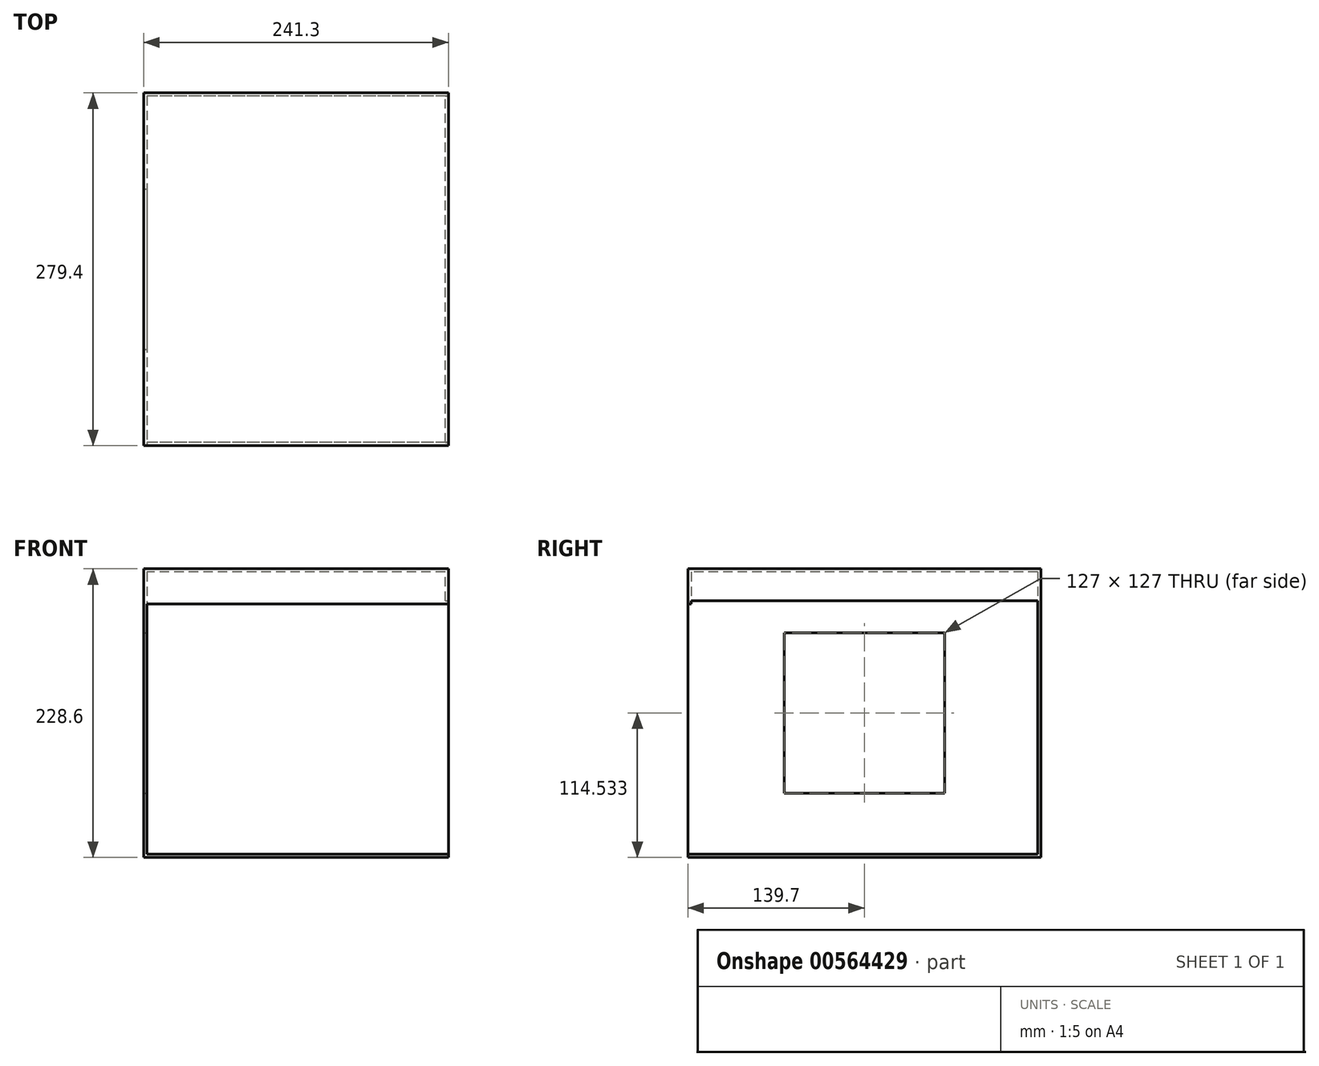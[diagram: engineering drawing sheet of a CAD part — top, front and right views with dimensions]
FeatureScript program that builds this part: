
annotation { "Feature Type Name" : "Feature", "Feature Type Description" : "" }
export const myFeature = defineFeature(function(context is Context, id is Id, definition is map)
    precondition{}
    {
        {
            var Q0;
            Q0=qCreatedBy(makeId("Top.planeOp"),FACE);
            var sketch = newSketch(context, id + "F0", { "sketchPlane" : qUnion([Q0])});
            skLineSegment(sketch, "E0.bottom", {"start": v(120.65, 139.7) * mm, "end": v(-120.65, 139.7) * mm});
            skLineSegment(sketch, "E0.top", {"start": v(120.65, -139.7) * mm, "end": v(-120.65, -139.7) * mm});
            skLineSegment(sketch, "E0.left", {"start": v(120.65, 139.7) * mm, "end": v(120.65, -139.7) * mm});
            skLineSegment(sketch, "E0.right", {"start": v(-120.65, 139.7) * mm, "end": v(-120.65, -139.7) * mm});
            skPoint(sketch, "E0.middle", {"position": v(0, 0) * mm});
            skSolve(sketch);
        }
        {
            var Q0;
            Q0 = qSketchRegion(id + "F0", true);
            extrude(context, id + "F1", {"entities" : qUnion([Q0]), "depth" : 228.6 * mm, "offsetDistance" : 25.4 * mm});
        }
        {
            var Q0;
            Q0=makeQuery(id+"F1.opExtrude","SWEPT_FACE",FACE,{"disambiguationData":[OSD([sQuery(id+"F0.wireOp",EDGE,"E0.top")])]});
            shell(context, id + "F2", {"entities" : qUnion([Q0]), "thickness" : 2.54 * mm});
        }
        {
            var Q0;
            Q0=makeQuery(id+"F2.opShell","OFFSET_FACE",FACE,{"disambiguationData":[OSD([sQuery(id+"F0.wireOp",EDGE,"E0.right")])]});
            var sketch = newSketch(context, id + "F3", { "sketchPlane" : qUnion([Q0])});
            skLineSegment(sketch, "E1.bottom", {"start": v(63.5, 178.03) * mm, "end": v(-63.5, 178.03) * mm});
            skLineSegment(sketch, "E1.top", {"start": v(63.5, 51.03) * mm, "end": v(-63.5, 51.03) * mm});
            skLineSegment(sketch, "E1.left", {"start": v(63.5, 178.03) * mm, "end": v(63.5, 51.03) * mm});
            skLineSegment(sketch, "E1.right", {"start": v(-63.5, 178.03) * mm, "end": v(-63.5, 51.03) * mm});
            skPoint(sketch, "E1.middle", {"position": v(0, 114.53) * mm});
            skSolve(sketch);
        }
        {
            var Q0;
            Q0=makeQuery(id+"F3.imprint","IMPRINT",FACE,{"disambiguationData":[TD([[makeQuery(id+"F3.imprint","IMPRINT",EDGE,{"derivedFrom":sQuery(id+"F3.wireOp",EDGE,"E1.bottom")}),1.0]])]});
            extrude(context, id + "F4", {"entities" : qUnion([Q0]), "operationType" : NewBodyOperationType.REMOVE, "oppositeDirection" : true, "depth" : 25.4 * mm, "offsetDistance" : 25.4 * mm});
        }
        {
            var Q0;
            Q0=makeQuery(id+"F1.opExtrude","SWEPT_FACE",FACE,{"disambiguationData":[OSD([sQuery(id+"F0.wireOp",EDGE,"E0.left")])]});
            var sketch = newSketch(context, id + "F5", { "sketchPlane" : qUnion([Q0])});
            skLineSegment(sketch, "E2", {"start": v(-139.7, 203.2) * mm, "end": v(137.16, 203.2) * mm});
            skLineSegment(sketch, "E3", {"start": v(137.16, 203.2) * mm, "end": v(137.16, 2.54) * mm});
            skLineSegment(sketch, "E4", {"start": v(-139.7, 203.2) * mm, "end": v(-139.7, 2.54) * mm});
            skLineSegment(sketch, "E5", {"start": v(-139.7, 2.54) * mm, "end": v(137.16, 2.54) * mm});
            skSolve(sketch);
        }
        {
            var Q0;
            Q0 = qSketchRegion(id + "F5", true);
            extrude(context, id + "F6", {"entities" : qUnion([Q0]), "operationType" : NewBodyOperationType.REMOVE, "oppositeDirection" : true, "depth" : 25.4 * mm, "offsetDistance" : 25.4 * mm});
        }
        {
            var Q0;
            Q0=makeQuery(id+"F2.opShell","OFFSET_FACE",FACE,{"disambiguationData":[OSD([sQuery(id+"F0.wireOp",EDGE,"E0.right")])]});
            var sketch = newSketch(context, id + "F7", { "sketchPlane" : qUnion([Q0])});
            skLineSegment(sketch, "E6", {"start": v(-139.7, 226.06) * mm, "end": v(-139.7, 200.66) * mm});
            skLineSegment(sketch, "E7", {"start": v(-137.16, 226.06) * mm, "end": v(-137.16, 200.66) * mm});
            skLineSegment(sketch, "E8", {"start": v(-137.16, 200.66) * mm, "end": v(-139.7, 200.66) * mm});
            skLineSegment(sketch, "E9", {"start": v(-137.16, 226.06) * mm, "end": v(-139.7, 226.06) * mm});
            skSolve(sketch);
        }
        {
            var Q0;
            Q0 = qSketchRegion(id + "F7", true);
            var Q1;
            Q1=makeQuery(id+"F1.opExtrude","SWEPT_FACE",FACE,{"disambiguationData":[OSD([sQuery(id+"F0.wireOp",EDGE,"E0.left")])]});
            extrude(context, id + "F8", {"entities" : qUnion([Q0]), "operationType" : NewBodyOperationType.ADD, "endBound" : BoundingType.UP_TO_SURFACE, "depth" : 25.4 * mm, "endBoundEntityFace" : qUnion([Q1]), "offsetDistance" : 25.4 * mm});
        }
    });
